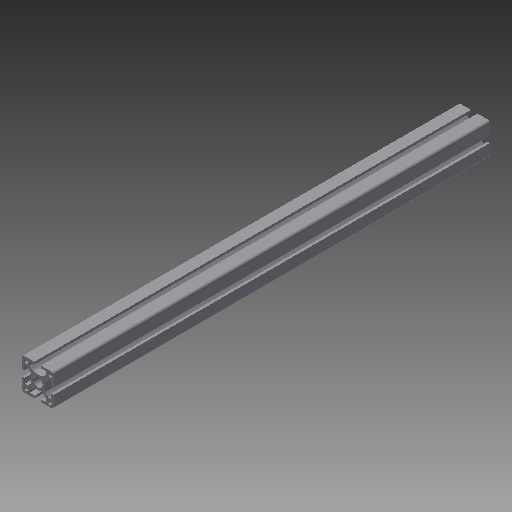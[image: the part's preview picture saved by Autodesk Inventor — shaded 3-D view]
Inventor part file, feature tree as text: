
AUTODESK INVENTOR PART (.ipt)
format: ipt  version: 2018 (Build 220112000, 112)  size: 222,208 bytes
history: native  units: mm
features: other x42, sketch x5, hole x4, extrude x1
ambient origin geometry x8: Origin, YZ Plane, XZ Plane, XY Plane, X Axis, Y Axis, Z Axis, Center Point
bodies: Solid1 (feature_tree)
feature tree (52):
  extrude  "Extrusion1"  [1 undecoded]
  hole  "Drilling 1"  [1 undecoded]
  hole  "Drilling 2"  [1 undecoded]
  hole  "Drilling 3"  [1 undecoded]
  hole  "Drilling 4"  [1 undecoded]
  other  "side_4d_XY"
  other  "side_4d_YZ"
  other  "side_4d_ZX"
  other  "side_4d_X"
  other  "side_4d_Y"
  other  "side_4d_Z"
  other  "side_4d_Center"
  other  "side_1a_XY"
  other  "side_1a_YZ"
  other  "side_1a_ZX"
  other  "side_1a_X"
  other  "side_1a_Y"
  other  "side_1a_Z"
  other  "side_1a_Center"
  other  "side_2b_XY"
  other  "side_2b_YZ"
  other  "side_2b_ZX"
  other  "side_2b_X"
  other  "side_2b_Y"
  other  "side_2b_Z"
  other  "side_2b_Center"
  other  "side_3c_XY"
  other  "side_3c_YZ"
  other  "side_3c_ZX"
  other  "side_3c_X"
  other  "side_3c_Y"
  other  "side_3c_Z"
  other  "side_3c_Center"
  other  "end_XY"
  other  "end_YZ"
  other  "end_ZX"
  other  "end_X"
  other  "end_Y"
  other  "end_Z"
  other  "end_Center"
  other  "start_XY"
  other  "start_YZ"
  other  "start_ZX"
  other  "start_X"
  other  "start_Y"
  other  "start_Z"
  other  "start_Center"
  sketch  "Skizze_1"  dims[d0=550.0mm d1=0.0mm]
  sketch  "Sketch2"  dims[d2=5.0mm d3=6.0mm d4=4.0mm d5=2.0mm d6=90.0deg d7=6000.0mm d8=0.0mm]
  sketch  "Sketch3"  dims[d9=5.0mm d10=6.0mm d11=4.0mm d12=2.0mm d13=90.0deg d14=6000.0mm d15=0.0mm]
  sketch  "Sketch4"  dims[d16=5.0mm d17=6.0mm d18=4.0mm d19=2.0mm d20=90.0deg d21=6000.0mm d22=0.0mm]
  sketch  "Sketch5"  dims[d23=5.0mm d24=6.0mm d25=4.0mm d26=2.0mm d27=90.0deg d28=6000.0mm d29=0.0mm]
note: 5 required parameter values undecoded (feature->parameter linkage not recoverable at this tier; creation-order binding heuristic only, values carry confidence <= 0.55)
